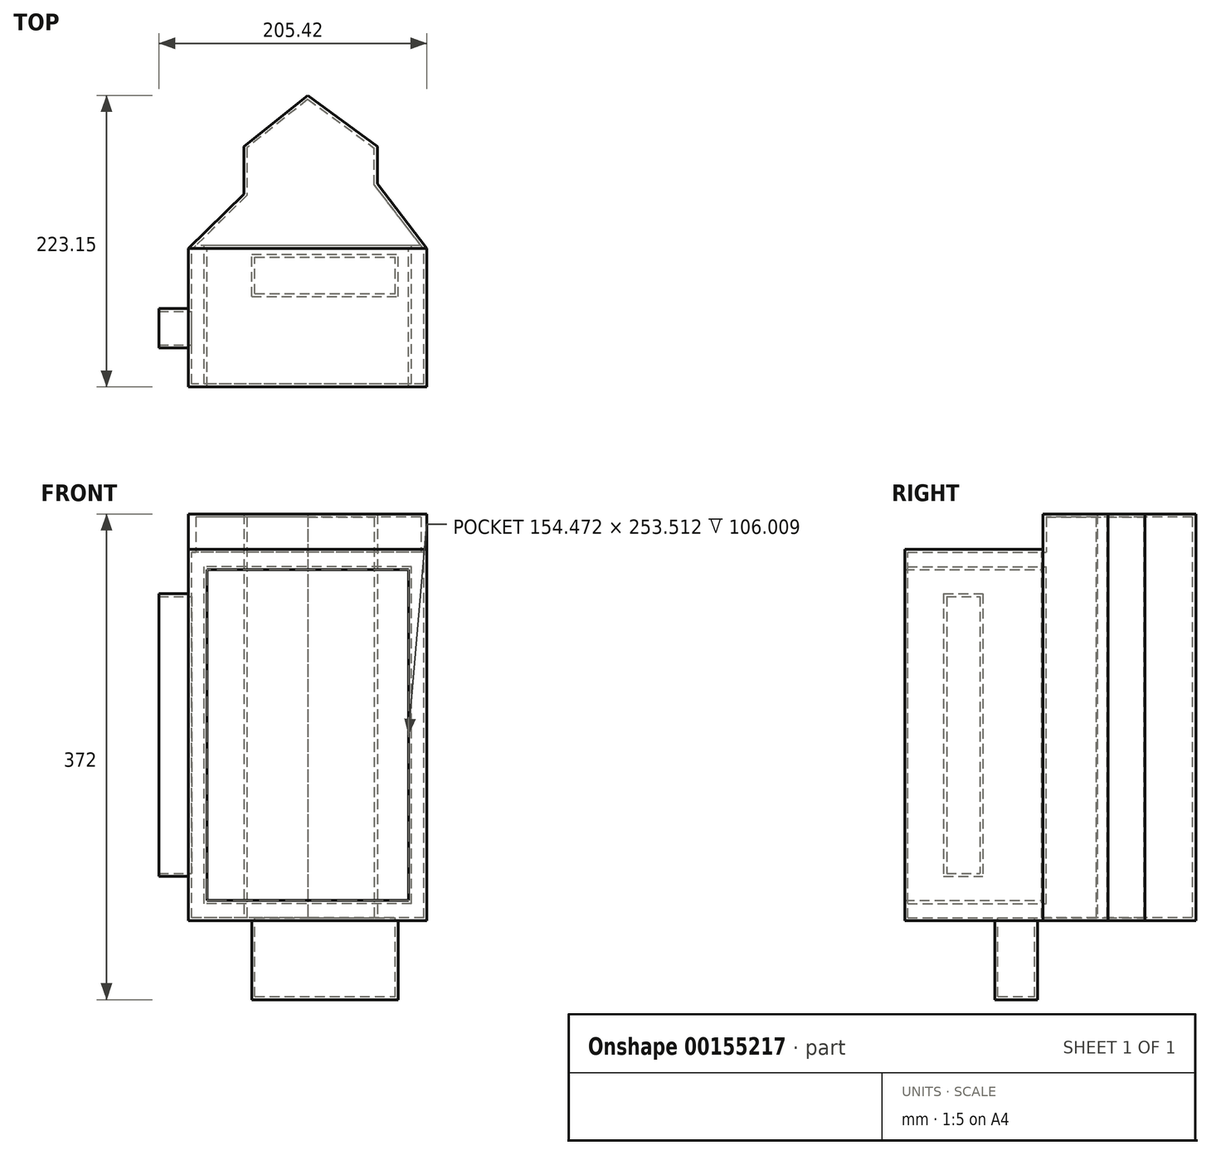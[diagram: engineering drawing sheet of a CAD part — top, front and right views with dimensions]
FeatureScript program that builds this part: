
annotation { "Feature Type Name" : "Feature", "Feature Type Description" : "" }
export const myFeature = defineFeature(function(context is Context, id is Id, definition is map)
    precondition{}
    {
        {
            var Q0;
            Q0=qCreatedBy(makeId("Front.planeOp"),FACE);
            var sketch = newSketch(context, id + "F0", { "sketchPlane" : qUnion([Q0])});
            skLineSegment(sketch, "E0.bottom", {"start": v(77.24, -126.76) * mm, "end": v(-77.24, -126.76) * mm});
            skLineSegment(sketch, "E0.top", {"start": v(77.24, 126.76) * mm, "end": v(-77.24, 126.76) * mm});
            skLineSegment(sketch, "E0.left", {"start": v(77.24, -126.76) * mm, "end": v(77.24, 126.76) * mm});
            skLineSegment(sketch, "E0.right", {"start": v(-77.24, -126.76) * mm, "end": v(-77.24, 126.76) * mm});
            skPoint(sketch, "E0.middle", {"position": v(0, 0) * mm});
            skLineSegment(sketch, "E1.bottom", {"start": v(91.28, -142.28) * mm, "end": v(-91.28, -142.28) * mm});
            skLineSegment(sketch, "E1.top", {"start": v(91.28, 142.28) * mm, "end": v(-91.28, 142.28) * mm});
            skLineSegment(sketch, "E1.left", {"start": v(91.28, -142.28) * mm, "end": v(91.28, 142.28) * mm});
            skLineSegment(sketch, "E1.right", {"start": v(-91.28, -142.28) * mm, "end": v(-91.28, 142.28) * mm});
            skLineSegment(sketch, "E2", {"start": v(77.24, 0) * mm, "end": v(91.28, 0) * mm});
            skSolve(sketch);
        }
        {
            var Q0;
            {var subQ3=sQuery(id+"F0.wireOp",EDGE,"E0.bottom");Q0=makeQuery(id+"F0.imprint","IMPRINT",FACE,{"disambiguationData":[TD([[makeQuery(id+"F0.imprint","IMPRINT",EDGE,{"derivedFrom":subQ3}),1.0]])]});}
            extrude(context, id + "F1", {"entities" : qUnion([Q0]), "depth" : 0.12 * yard});
        }
        {
            var Q0;
            Q0=makeQuery(id+"F1.opExtrude","SWEPT_FACE",FACE,{"disambiguationData":[OSD([sQuery(id+"F0.wireOp",EDGE,"E1.bottom")])]});
            var sketch = newSketch(context, id + "F2", { "sketchPlane" : qUnion([Q0])});
            skLineSegment(sketch, "E3", {"start": v(-91.28, 0) * mm, "end": v(91.28, 0) * mm});
            skLineSegment(sketch, "E4", {"start": v(91.28, 0) * mm, "end": v(53.23, -49.62) * mm});
            skLineSegment(sketch, "E5", {"start": v(53.23, -49.62) * mm, "end": v(53.23, -78.11) * mm});
            skLineSegment(sketch, "E6", {"start": v(53.23, -78.11) * mm, "end": v(-48.93, -78.11) * mm});
            skLineSegment(sketch, "E7", {"start": v(-48.93, -78.11) * mm, "end": v(-48.93, -41.55) * mm});
            skLineSegment(sketch, "E8", {"start": v(-48.93, -41.55) * mm, "end": v(-91.28, 0) * mm});
            skLineSegment(sketch, "E9", {"start": v(0, -117.14) * mm, "end": v(53.23, -78.11) * mm});
            skLineSegment(sketch, "E10", {"start": v(0, -117.14) * mm, "end": v(-48.93, -78.11) * mm});
            skSolve(sketch);
        }
        {
            var Q0;
            Q0 = qSketchRegion(id + "F2", true);
            extrude(context, id + "F3", {"entities" : qUnion([Q0]), "operationType" : NewBodyOperationType.ADD, "oppositeDirection" : true, "depth" : 0.34 * yard});
        }
        {
            var Q0;
            Q0=makeQuery(id+"F3.boolean.opBoolean","MERGE",FACE,{"derivedFrom":[makeQuery(id+"F1.opExtrude","SWEPT_FACE",FACE,{"disambiguationData":[OSD([sQuery(id+"F0.wireOp",EDGE,"E1.bottom")])]}),makeQuery(id+"F3.opExtrude","CAP_FACE",FACE,{"disambiguationData":[OSD([sQuery(id+"F2.wireOp",EDGE,"E3"),sQuery(id+"F2.wireOp",EDGE,"E4"),sQuery(id+"F2.wireOp",EDGE,"E5"),sQuery(id+"F2.wireOp",EDGE,"E7"),sQuery(id+"F2.wireOp",EDGE,"E8"),sQuery(id+"F2.wireOp",EDGE,"E9"),sQuery(id+"F2.wireOp",EDGE,"E10")])],"isStart":true})]});
            var sketch = newSketch(context, id + "F4", { "sketchPlane" : qUnion([Q0])});
            skLineSegment(sketch, "E11.bottom", {"start": v(-42.9, 36.96) * mm, "end": v(69.17, 36.96) * mm});
            skLineSegment(sketch, "E11.top", {"start": v(-42.9, 4.36) * mm, "end": v(69.17, 4.36) * mm});
            skLineSegment(sketch, "E11.left", {"start": v(-42.9, 36.96) * mm, "end": v(-42.9, 4.36) * mm});
            skLineSegment(sketch, "E11.right", {"start": v(69.17, 36.96) * mm, "end": v(69.17, 4.36) * mm});
            skPoint(sketch, "E11.middle", {"position": v(13.13, 20.66) * mm});
            skSolve(sketch);
        }
        {
            var Q0;
            Q0=makeQuery(id+"F4.imprint","IMPRINT",FACE,{"disambiguationData":[TD([[makeQuery(id+"F4.imprint","IMPRINT",EDGE,{"derivedFrom":sQuery(id+"F4.wireOp",EDGE,"E11.bottom")}),-1.0]])]});
            extrude(context, id + "F5", {"entities" : qUnion([Q0]), "operationType" : NewBodyOperationType.ADD, "depth" : 0.07 * yard});
        }
        {
            var Q0;
            Q0=makeQuery(id+"F1.opExtrude","SWEPT_FACE",FACE,{"disambiguationData":[OSD([sQuery(id+"F0.wireOp",EDGE,"E1.right")])]});
            var sketch = newSketch(context, id + "F6", { "sketchPlane" : qUnion([Q0])});
            skLineSegment(sketch, "E12.bottom", {"start": v(76.27, 108.26) * mm, "end": v(46.06, 108.26) * mm});
            skLineSegment(sketch, "E12.top", {"start": v(76.27, -108.26) * mm, "end": v(46.06, -108.26) * mm});
            skLineSegment(sketch, "E12.left", {"start": v(76.27, 108.26) * mm, "end": v(76.27, -108.26) * mm});
            skLineSegment(sketch, "E12.right", {"start": v(46.06, 108.26) * mm, "end": v(46.06, -108.26) * mm});
            skPoint(sketch, "E12.middle", {"position": v(61.16, 0) * mm});
            skSolve(sketch);
        }
        {
            var Q0;
            Q0=makeQuery(id+"F6.imprint","IMPRINT",FACE,{"disambiguationData":[TD([[makeQuery(id+"F6.imprint","IMPRINT",EDGE,{"derivedFrom":sQuery(id+"F6.wireOp",EDGE,"E12.bottom")}),1.0]])]});
            extrude(context, id + "F7", {"entities" : qUnion([Q0]), "operationType" : NewBodyOperationType.ADD, "depth" : 0.03 * yard});
        }
        {
            var Q0;
            Q0=makeQuery(id+"F7.opExtrude","CAP_FACE",FACE,{"disambiguationData":[OSD([sQuery(id+"F6.wireOp",EDGE,"E12.bottom"),sQuery(id+"F6.wireOp",EDGE,"E12.top"),sQuery(id+"F6.wireOp",EDGE,"E12.left"),sQuery(id+"F6.wireOp",EDGE,"E12.right")])],"isStart":false});
            shell(context, id + "F8", {"entities" : qUnion([Q0]), "thickness" : 0 * yard});
        }
    });
